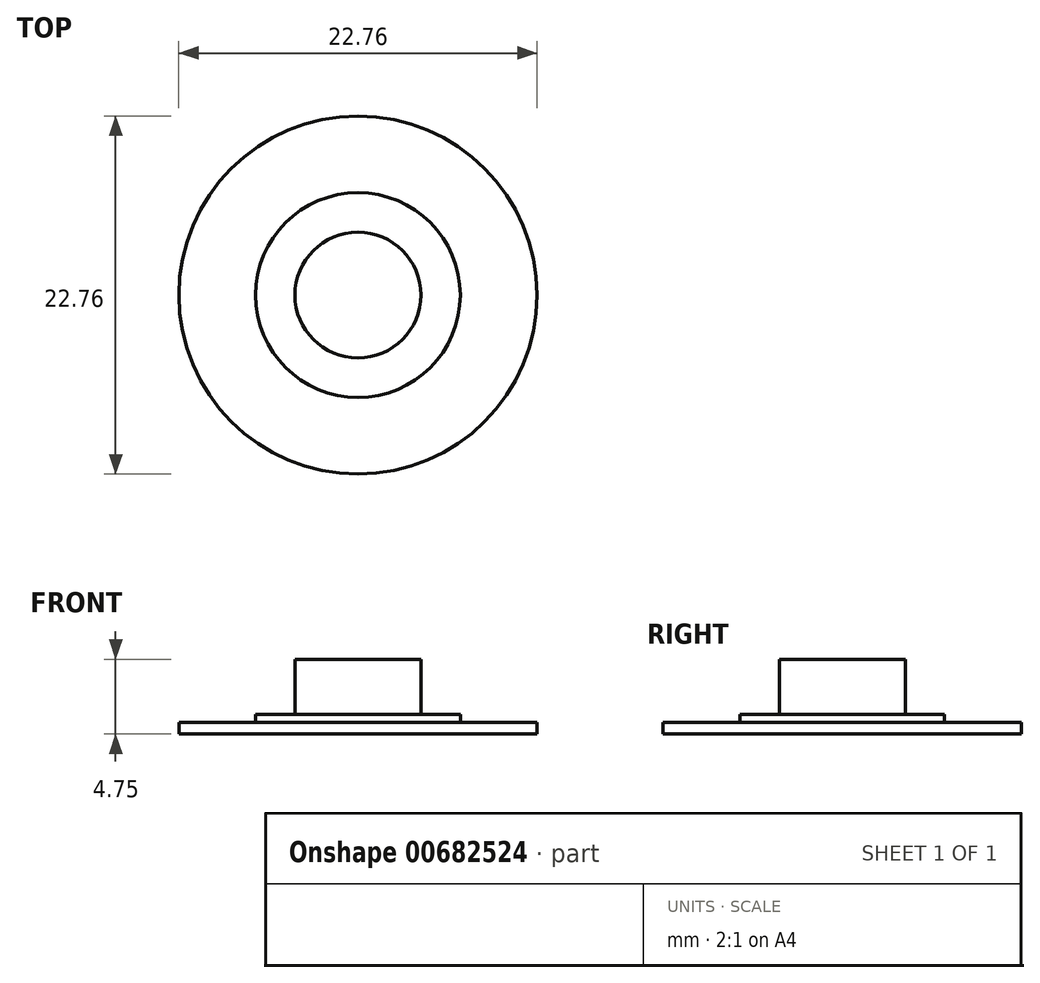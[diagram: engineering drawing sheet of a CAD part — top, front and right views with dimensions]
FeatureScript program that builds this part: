
annotation { "Feature Type Name" : "Feature", "Feature Type Description" : "" }
export const myFeature = defineFeature(function(context is Context, id is Id, definition is map)
    precondition{}
    {
        {
            var Q0;
            Q0=qCreatedBy(makeId("Top.planeOp"),FACE);
            var sketch = newSketch(context, id + "F0", { "sketchPlane" : qUnion([Q0])});
            skCircle(sketch, "E0", {"center": v(0, 0) * mm, "radius": 4 * mm});
            skCircle(sketch, "E1", {"center": v(0, 0) * mm, "radius": 6.5 * mm});
            skCircle(sketch, "E2", {"center": v(0, 0) * mm, "radius": 11.38 * mm});
            skSolve(sketch);
        }
        {
            var Q0;
            Q0=makeQuery(id+"F0.imprint","IMPRINT",FACE,{"disambiguationData":[TD([[makeQuery(id+"F0.imprint","IMPRINT",EDGE,{"derivedFrom":sQuery(id+"F0.wireOp",EDGE,"E1")}),-1.0]])]});
            extrude(context, id + "F1", {"entities" : qUnion([Q0]), "depth" : .75 * mm, "offsetDistance" : 25.4 * mm});
        }
        {
            var Q0;
            Q0=makeQuery(id+"F0.imprint","IMPRINT",FACE,{"disambiguationData":[TD([[makeQuery(id+"F0.imprint","IMPRINT",EDGE,{"derivedFrom":sQuery(id+"F0.wireOp",EDGE,"E0")}),-1.0]])]});
            extrude(context, id + "F2", {"entities" : qUnion([Q0]), "operationType" : NewBodyOperationType.ADD, "depth" : 1.25 * mm, "offsetDistance" : 25.4 * mm});
        }
        {
            var Q0;
            Q0=makeQuery(id+"F0.imprint","IMPRINT",FACE,{"disambiguationData":[TD([[makeQuery(id+"F0.imprint","IMPRINT",EDGE,{"derivedFrom":sQuery(id+"F0.wireOp",EDGE,"E0")}),1.0]])]});
            extrude(context, id + "F3", {"entities" : qUnion([Q0]), "operationType" : NewBodyOperationType.ADD, "depth" : 4.75 * mm, "offsetDistance" : 25.4 * mm});
        }
    });
